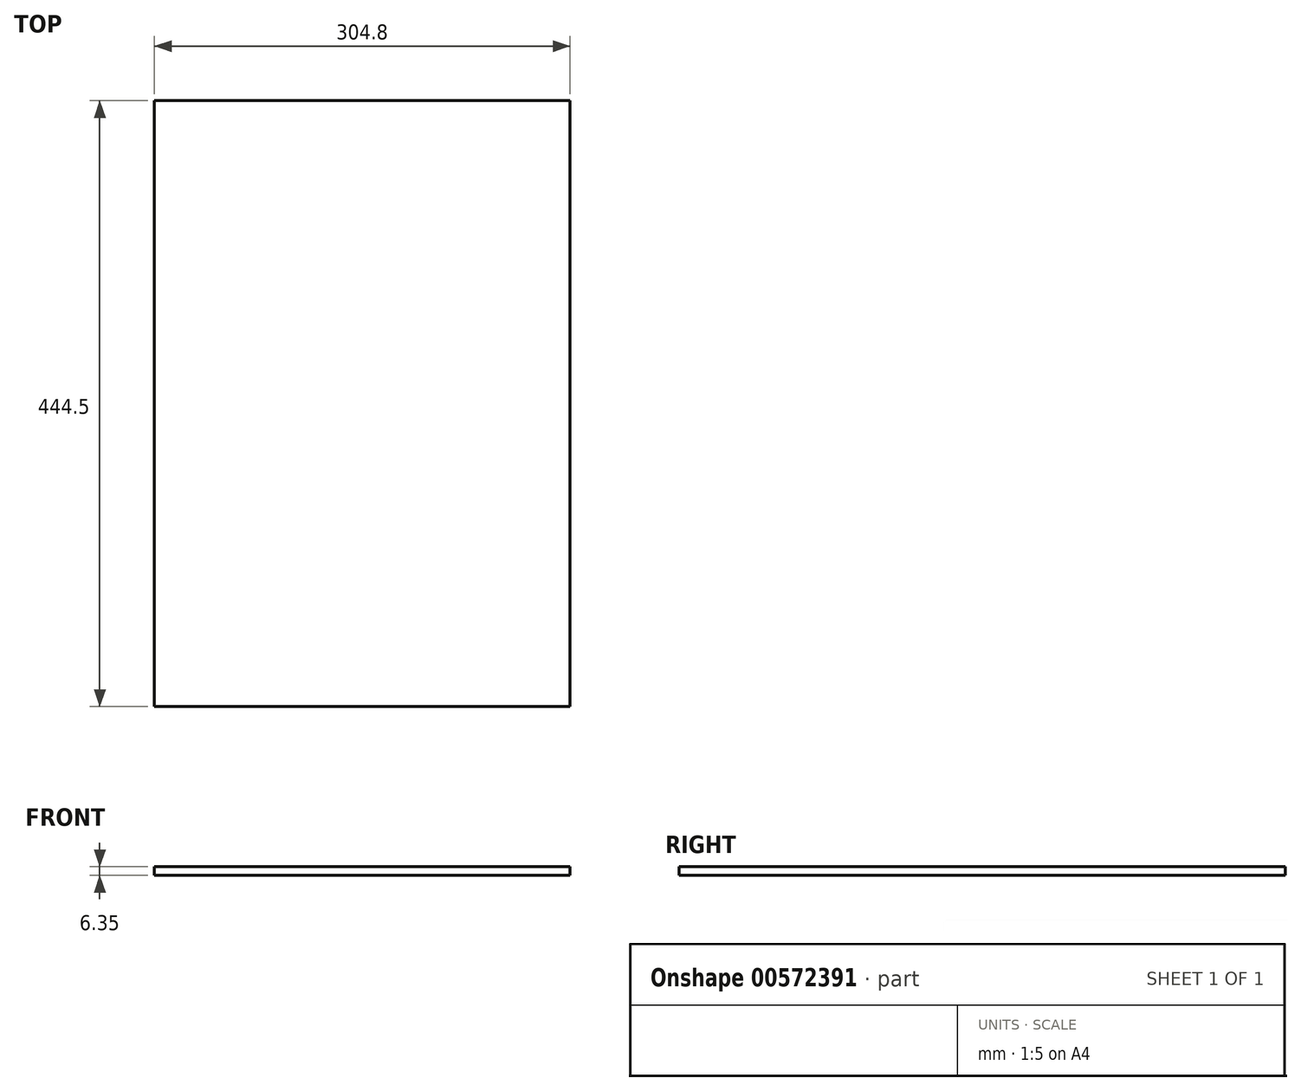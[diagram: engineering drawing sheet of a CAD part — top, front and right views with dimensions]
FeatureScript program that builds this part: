
annotation { "Feature Type Name" : "Feature", "Feature Type Description" : "" }
export const myFeature = defineFeature(function(context is Context, id is Id, definition is map)
    precondition{}
    {
        {
            var Q0;
            Q0=qCreatedBy(makeId("Top.planeOp"),FACE);
            var sketch = newSketch(context, id + "F0", { "sketchPlane" : qUnion([Q0])});
            skLineSegment(sketch, "E0.bottom", {"start": v(0, 0) * mm, "end": v(-304.8, 0) * mm});
            skLineSegment(sketch, "E0.top", {"start": v(0, 444.5) * mm, "end": v(-304.8, 444.5) * mm});
            skLineSegment(sketch, "E0.left", {"start": v(0, 0) * mm, "end": v(0, 444.5) * mm});
            skLineSegment(sketch, "E0.right", {"start": v(-304.8, 0) * mm, "end": v(-304.8, 444.5) * mm});
            skSolve(sketch);
        }
        {
            var Q0;
            Q0 = qSketchRegion(id + "F0", true);
            extrude(context, id + "F1", {"entities" : qUnion([Q0]), "depth" : 6.35 * mm, "offsetDistance" : 25.4 * mm});
        }
    });
